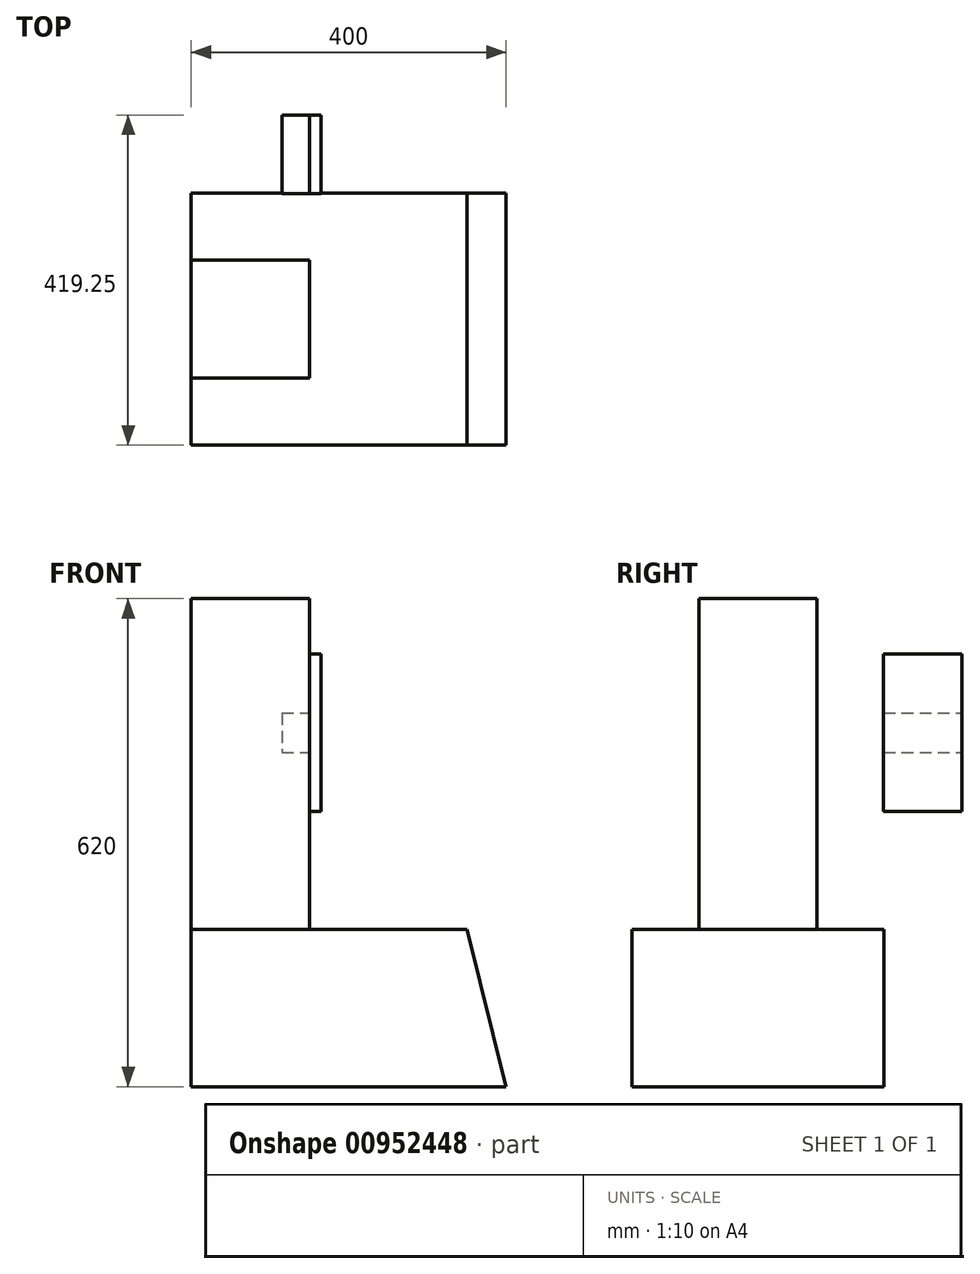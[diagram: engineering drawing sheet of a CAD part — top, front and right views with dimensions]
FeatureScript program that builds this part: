
annotation { "Feature Type Name" : "Feature", "Feature Type Description" : "" }
export const myFeature = defineFeature(function(context is Context, id is Id, definition is map)
    precondition{}
    {
        {
            var Q0;
            Q0=qCreatedBy(makeId("Front.planeOp"),FACE);
            var sketch = newSketch(context, id + "F0", { "sketchPlane" : qUnion([Q0])});
            skLineSegment(sketch, "E0.bottom", {"start": v(0, 0) * mm, "end": v(400, 0) * mm});
            skLineSegment(sketch, "E0.top", {"start": v(0, 200) * mm, "end": v(350, 200) * mm});
            skLineSegment(sketch, "E0.left", {"start": v(0, 0) * mm, "end": v(0, 200) * mm});
            skLineSegment(sketch, "E1", {"start": v(400, 0) * mm, "end": v(350, 200) * mm});
            skSolve(sketch);
        }
        {
            var Q0;
            Q0 = qSketchRegion(id + "F0", true);
            extrude(context, id + "F1", {"entities" : qUnion([Q0]), "oppositeDirection" : true, "depth" : 320 * mm, "offsetDistance" : 25 * mm});
        }
        {
            var Q0;
            Q0=makeQuery(id+"F1.opExtrude","SWEPT_FACE",FACE,{"disambiguationData":[OSD([sQuery(id+"F0.wireOp",EDGE,"E0.top")])]});
            var sketch = newSketch(context, id + "F2", { "sketchPlane" : qUnion([Q0])});
            skLineSegment(sketch, "E2.bottom", {"start": v(0, 235) * mm, "end": v(150, 235) * mm});
            skLineSegment(sketch, "E2.top", {"start": v(0, 85) * mm, "end": v(150, 85) * mm});
            skLineSegment(sketch, "E2.left", {"start": v(0, 235) * mm, "end": v(0, 85) * mm});
            skLineSegment(sketch, "E2.right", {"start": v(150, 235) * mm, "end": v(150, 85) * mm});
            skPoint(sketch, "E2.middle", {"position": v(75, 160) * mm});
            skSolve(sketch);
        }
        {
            var Q0;
            Q0 = qSketchRegion(id + "F2", true);
            extrude(context, id + "F3", {"entities" : qUnion([Q0]), "operationType" : NewBodyOperationType.ADD, "depth" : 420 * mm, "offsetDistance" : 25 * mm});
        }
        {
            var Q0;
            Q0=makeQuery(id+"F3.opExtrude","SWEPT_FACE",FACE,{"disambiguationData":[OSD([sQuery(id+"F2.wireOp",EDGE,"E2.right")])]});
            var sketch = newSketch(context, id + "F4", { "sketchPlane" : qUnion([Q0])});
            skLineSegment(sketch, "E3.bottom", {"start": v(319.25, 549.77) * mm, "end": v(419.25, 549.77) * mm});
            skLineSegment(sketch, "E3.top", {"start": v(319.25, 349.77) * mm, "end": v(419.25, 349.77) * mm});
            skLineSegment(sketch, "E3.left", {"start": v(319.25, 549.77) * mm, "end": v(319.25, 349.77) * mm});
            skLineSegment(sketch, "E3.right", {"start": v(419.25, 549.77) * mm, "end": v(419.25, 349.77) * mm});
            skPoint(sketch, "E3.middle", {"position": v(369.25, 449.77) * mm});
            skLineSegment(sketch, "E4.bottom", {"start": v(319.25, 474.77) * mm, "end": v(419.25, 474.77) * mm});
            skLineSegment(sketch, "E4.top", {"start": v(319.25, 424.77) * mm, "end": v(419.25, 424.77) * mm});
            skLineSegment(sketch, "E4.left", {"start": v(319.25, 474.77) * mm, "end": v(319.25, 424.77) * mm});
            skLineSegment(sketch, "E4.right", {"start": v(419.25, 474.77) * mm, "end": v(419.25, 424.77) * mm});
            skSolve(sketch);
        }
        {
            var Q0;
            {var subQ3=sQuery(id+"F4.wireOp",EDGE,"E4.bottom");var subQ9=makeQuery(id+"F4.imprint","IMPRINT",EDGE,{"derivedFrom":subQ3});var subQ10=sQuery(id+"F4.wireOp",EDGE,"E3.top");var subQ11=sQuery(id+"F4.wireOp",EDGE,"E3.bottom");Q0=qUnion([makeQuery(id+"F4.imprint","IMPRINT",FACE,{"disambiguationData":[TD([[makeQuery(id+"F4.imprint","IMPRINT",EDGE,{"derivedFrom":subQ11}),-1.0]])]}),makeQuery(id+"F4.imprint","IMPRINT",FACE,{"disambiguationData":[TD([[makeQuery(id+"F4.imprint","IMPRINT",EDGE,{"derivedFrom":subQ10}),1.0]])]}),makeQuery(id+"F4.imprint","IMPRINT",FACE,{"disambiguationData":[TD([[subQ9,-1.0]])]})]);}
            extrude(context, id + "F5", {"entities" : qUnion([Q0]), "depth" : 15 * mm, "offsetDistance" : 25 * mm});
        }
        {
            var Q0;
            {var subQ2=sQuery(id+"F4.wireOp",EDGE,"E4.bottom");Q0=makeQuery(id+"F4.imprint","IMPRINT",FACE,{"disambiguationData":[TD([[makeQuery(id+"F4.imprint","IMPRINT",EDGE,{"derivedFrom":subQ2}),-1.0]])]});}
            extrude(context, id + "F6", {"entities" : qUnion([Q0]), "operationType" : NewBodyOperationType.ADD, "oppositeDirection" : true, "depth" : 35 * mm, "offsetDistance" : 25 * mm});
        }
    });
